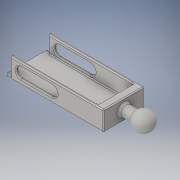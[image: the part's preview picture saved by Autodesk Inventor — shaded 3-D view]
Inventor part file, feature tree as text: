
AUTODESK INVENTOR PART (.ipt)
format: ipt  version: 2016 (Build 200138000, 138)  size: 291,328 bytes
history: native  units: mm
features: projected_geometry x9, sketch x6, extrude x5, fillet x3, other x1, plane x1, revolve x1
ambient origin geometry x8: Origin, YZ Plane, XZ Plane, XY Plane, X Axis, Y Axis, Z Axis, Center Point
bodies: Solid1 (feature_tree)
feature tree (26):
  extrude  "Extrusion1"  Depth=17.0mm
  extrude  "Extrusion2"  Depth=4.0mm
  other  "Work Axis1"
  plane  "Work Plane1"
  revolve  "Revolution1"  [1 undecoded]
  extrude  "Extrusion3"  Depth=9.5mm
  extrude  "Extrusion4"  Depth=1.5mm
  fillet  "Fillet4"  Radius=10.0mm
  fillet  "Fillet5"  Radius=1.5mm
  extrude  "Extrusion5"  Depth=1.0mm
  fillet  "Fillet6"  Radius=0.5mm
  sketch  "Sketch1"  dims[d0=17.0mm d1=19.8mm]
  sketch  "Sketch2"  dims[d2=45.0mm d3=4.0mm]
  projected_geometry  "Projected Loop1"
  sketch  "Sketch3"  dims[d4=9.5mm d5=0.0mm d6=5.0mm]
  projected_geometry  "Projected Loop2"
  sketch  "Sketch4"  dims[d7=9.5mm d8=0.0mm d9=4.5mm]
  projected_geometry  "Projected Loop3"
  sketch  "Sketch5"  dims[d10=90.0deg d14=1.5mm d15=10.0mm d16=0.0mm d17=1.5mm]
  projected_geometry  "Projected Loop4"
  sketch  "Sketch6"  dims[d18=2.0mm d19=0.0mm d20=1.0mm d21=0.5mm d22=5.0mm d23=5.0mm d24=5.0mm d25=15.0mm d26=2.0mm d27=0.0mm d28=0.5mm]
  projected_geometry  "Projected Loop5"
  projected_geometry  "Projected Loop6"
  projected_geometry  "Projected Loop7"
  projected_geometry  "Projected Loop8"
  projected_geometry  "Projected Loop9"
note: 1 required parameter value undecoded (feature->parameter linkage not recoverable at this tier; creation-order binding heuristic only, values carry confidence <= 0.55)
